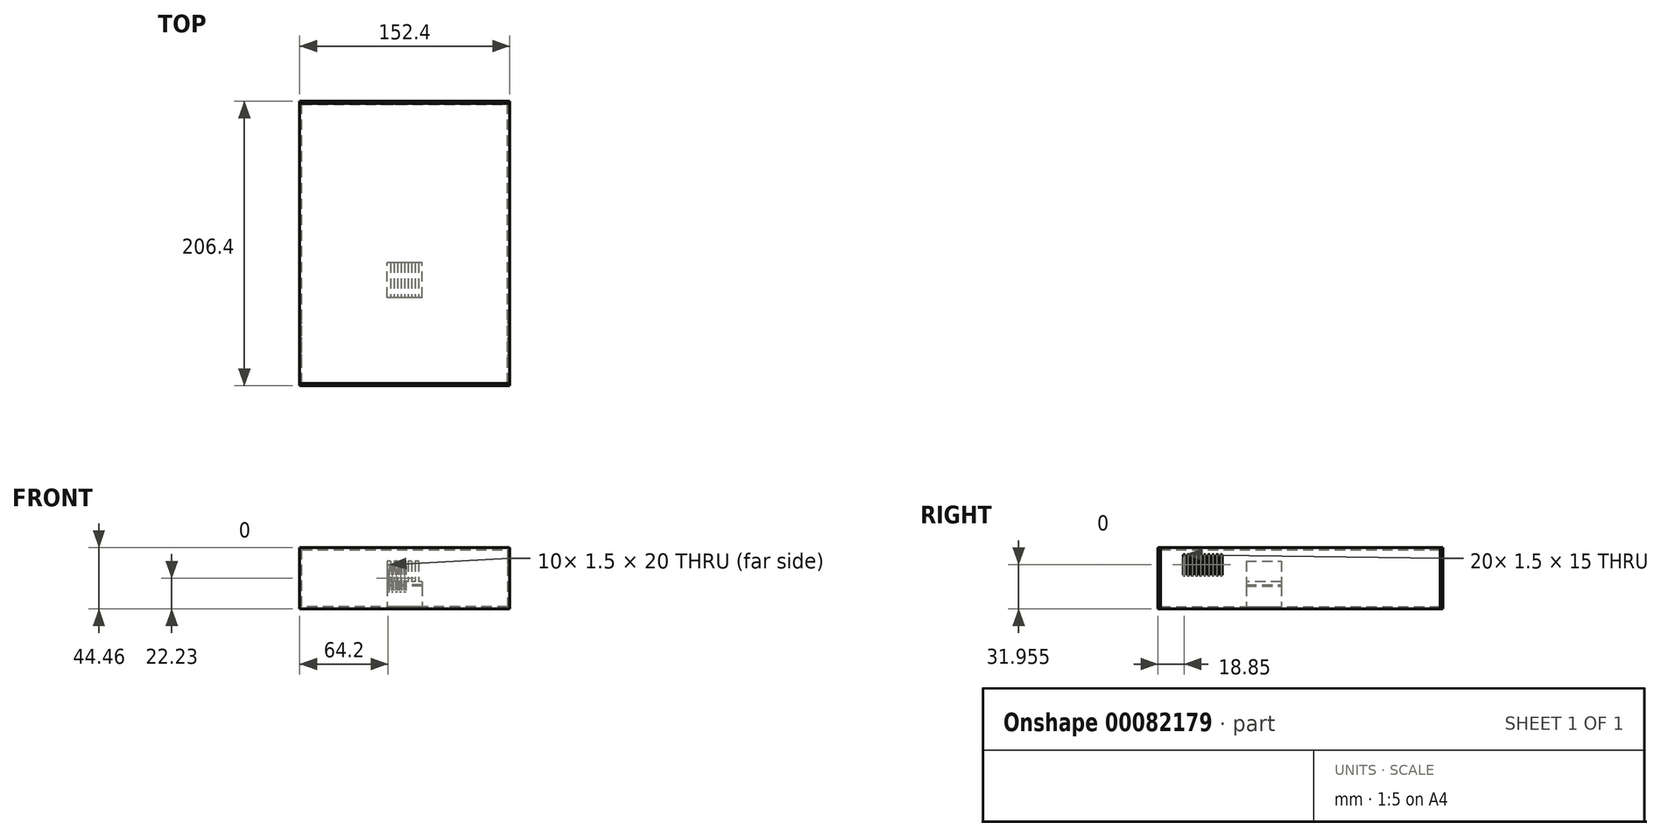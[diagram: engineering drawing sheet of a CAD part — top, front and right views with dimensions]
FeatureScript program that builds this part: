
annotation { "Feature Type Name" : "Feature", "Feature Type Description" : "" }
export const myFeature = defineFeature(function(context is Context, id is Id, definition is map)
    precondition{}
    {
        {
            var Q0;
            Q0=qCreatedBy(makeId("Front.planeOp"),FACE);
            var sketch = newSketch(context, id + "F0", { "sketchPlane" : qUnion([Q0])});
            skLineSegment(sketch, "E0.bottom", {"start": v(76.2, 22.22) * mm, "end": v(-76.2, 22.22) * mm});
            skLineSegment(sketch, "E0.top", {"start": v(76.2, -22.23) * mm, "end": v(-76.2, -22.23) * mm});
            skLineSegment(sketch, "E0.left", {"start": v(76.2, 22.22) * mm, "end": v(76.2, -22.23) * mm});
            skLineSegment(sketch, "E0.right", {"start": v(-76.2, 22.22) * mm, "end": v(-76.2, -22.23) * mm});
            skPoint(sketch, "E0.middle", {"position": v(0, 0) * mm});
            skSolve(sketch);
        }
        {
            var Q0;
            Q0 = qSketchRegion(id + "F0", true);
            extrude(context, id + "F1", {"entities" : qUnion([Q0]), "oppositeDirection" : true, "depth" : 203.2 * mm});
        }
        {
            var Q0;
            Q0=makeQuery(id+"F1.opExtrude","CAP_FACE",FACE,{"disambiguationData":[OSD([sQuery(id+"F0.wireOp",EDGE,"E0.bottom"),sQuery(id+"F0.wireOp",EDGE,"E0.top"),sQuery(id+"F0.wireOp",EDGE,"E0.left"),sQuery(id+"F0.wireOp",EDGE,"E0.right")])],"isStart":false});
            var sketch = newSketch(context, id + "F2", { "sketchPlane" : qUnion([Q0])});
            skLineSegment(sketch, "E1.0", {"start": v(-74.6, -20.62) * mm, "end": v(-74.6, 20.62) * mm});
            skLineSegment(sketch, "E1.1", {"start": v(74.6, -20.62) * mm, "end": v(-74.6, -20.62) * mm});
            skLineSegment(sketch, "E1.2", {"start": v(74.6, 20.62) * mm, "end": v(74.6, -20.62) * mm});
            skLineSegment(sketch, "E1.3", {"start": v(-74.6, 20.62) * mm, "end": v(74.6, 20.62) * mm});
            skSolve(sketch);
        }
        {
            var Q0;
            Q0 = qSketchRegion(id + "F2", true);
            extrude(context, id + "F3", {"entities" : qUnion([Q0]), "operationType" : NewBodyOperationType.REMOVE, "endBound" : BoundingType.THROUGH_ALL, "oppositeDirection" : true, "depth" : 25 * mm});
        }
        {
            var Q0;
            Q0=makeQuery(id+"F1.opExtrude","CAP_FACE",FACE,{"disambiguationData":[OSD([sQuery(id+"F0.wireOp",EDGE,"E0.bottom"),sQuery(id+"F0.wireOp",EDGE,"E0.top"),sQuery(id+"F0.wireOp",EDGE,"E0.left"),sQuery(id+"F0.wireOp",EDGE,"E0.right")])],"isStart":false});
            var sketch = newSketch(context, id + "F4", { "sketchPlane" : qUnion([Q0])});
            skSolve(sketch);
        }
        {
            var Q0;
            Q0=makeQuery(id+"F4.imprint","IMPRINT",FACE,{"disambiguationData":[TD([[makeQuery(id+"F4.imprint","IMPRINT",EDGE,{"derivedFrom":makeQuery(id+"F1.opExtrude","CAP_EDGE",EDGE,{"disambiguationData":[OSD([sQuery(id+"F0.wireOp",EDGE,"E0.bottom")])],"isStart":false})}),-1.0]])]});
            var sketch = newSketch(context, id + "F5", { "sketchPlane" : qUnion([Q0])});
            skLineSegment(sketch, "E2.0", {"start": v(-76.2, 22.22) * mm, "end": v(76.2, 22.22) * mm});
            skLineSegment(sketch, "E3.0", {"start": v(76.2, 22.22) * mm, "end": v(76.2, -22.23) * mm});
            skLineSegment(sketch, "E4.0", {"start": v(-76.2, -22.23) * mm, "end": v(76.2, -22.23) * mm});
            skLineSegment(sketch, "E5.0", {"start": v(-76.2, 22.22) * mm, "end": v(-76.2, -22.23) * mm});
            skSolve(sketch);
        }
        {
            var Q0;
            Q0 = qSketchRegion(id + "F5", true);
            var Q1;
            Q1=makeQuery(id+"F4.imprint","IMPRINT",FACE,{"disambiguationData":[TD([[makeQuery(id+"F4.imprint","IMPRINT",EDGE,{"derivedFrom":makeQuery(id+"F3.boolean.opBoolean","COPY",EDGE,{"derivedFrom":makeQuery(id+"F3.opExtrude","CAP_EDGE",EDGE,{"disambiguationData":[OSD([sQuery(id+"F2.wireOp",EDGE,"E1.0")])],"isStart":true})})}),-1.0]])]});
            extrude(context, id + "F6", {"entities" : qUnion([Q0, Q1]), "operationType" : NewBodyOperationType.ADD, "oppositeDirection" : true, "depth" : .63 * mm});
        }
        {
            var Q0;
            Q0=makeQuery(id+"F1.opExtrude","CAP_FACE",FACE,{"disambiguationData":[OSD([sQuery(id+"F0.wireOp",EDGE,"E0.bottom"),sQuery(id+"F0.wireOp",EDGE,"E0.top"),sQuery(id+"F0.wireOp",EDGE,"E0.left"),sQuery(id+"F0.wireOp",EDGE,"E0.right")])],"isStart":false});
            var sketch = newSketch(context, id + "F7", { "sketchPlane" : qUnion([Q0])});
            skLineSegment(sketch, "E6.0", {"start": v(-76.2, 22.22) * mm, "end": v(-76.2, -22.23) * mm});
            skLineSegment(sketch, "E6.1", {"start": v(-76.2, 22.22) * mm, "end": v(76.2, 22.22) * mm});
            skLineSegment(sketch, "E6.2", {"start": v(76.2, 22.22) * mm, "end": v(76.2, -22.23) * mm});
            skLineSegment(sketch, "E6.3", {"start": v(-76.2, -22.23) * mm, "end": v(76.2, -22.23) * mm});
            skSolve(sketch);
        }
        {
            var Q0;
            Q0 = qSketchRegion(id + "F7", true);
            extrude(context, id + "F8", {"entities" : qUnion([Q0]), "depth" : 1.6 * mm});
        }
        {
            var Q0;
            Q0=makeQuery(id+"F1.opExtrude","CAP_FACE",FACE,{"disambiguationData":[OSD([sQuery(id+"F0.wireOp",EDGE,"E0.bottom"),sQuery(id+"F0.wireOp",EDGE,"E0.top"),sQuery(id+"F0.wireOp",EDGE,"E0.left"),sQuery(id+"F0.wireOp",EDGE,"E0.right")])],"isStart":true});
            var sketch = newSketch(context, id + "F9", { "sketchPlane" : qUnion([Q0])});
            skLineSegment(sketch, "E7.0.0", {"start": v(76.2, -22.23) * mm, "end": v(76.2, 22.22) * mm});
            skLineSegment(sketch, "E7.0.1", {"start": v(76.2, 22.22) * mm, "end": v(-76.2, 22.22) * mm});
            skLineSegment(sketch, "E7.0.2", {"start": v(-76.2, 22.22) * mm, "end": v(-76.2, -22.23) * mm});
            skLineSegment(sketch, "E7.0.3", {"start": v(-76.2, -22.23) * mm, "end": v(76.2, -22.23) * mm});
            skSolve(sketch);
        }
        {
            var Q0;
            Q0 = qSketchRegion(id + "F9", true);
            extrude(context, id + "F10", {"entities" : qUnion([Q0]), "depth" : 1.6 * mm});
        }
        {
            var Q0;
            Q0=makeQuery(id+"F1.opExtrude","SWEPT_FACE",FACE,{"disambiguationData":[OSD([sQuery(id+"F0.wireOp",EDGE,"E0.right")])]});
            var sketch = newSketch(context, id + "F11", { "sketchPlane" : qUnion([Q0])});
            skLineSegment(sketch, "E8.bottom", {"start": v(-45, 17.22) * mm, "end": v(-43.5, 17.22) * mm});
            skLineSegment(sketch, "E8.top", {"start": v(-45, 2.22) * mm, "end": v(-43.5, 2.22) * mm});
            skLineSegment(sketch, "E8.left", {"start": v(-45, 17.22) * mm, "end": v(-45, 2.22) * mm});
            skLineSegment(sketch, "E8.right", {"start": v(-43.5, 17.22) * mm, "end": v(-43.5, 2.22) * mm});
            skLineSegment(sketch, "E9.1.0.0", {"start": v(-40.5, 17.22) * mm, "end": v(-40.5, 2.22) * mm});
            skLineSegment(sketch, "E9.1.0.1", {"start": v(-42, 17.22) * mm, "end": v(-42, 2.22) * mm});
            skLineSegment(sketch, "E9.1.0.2", {"start": v(-42, 2.22) * mm, "end": v(-40.5, 2.22) * mm});
            skLineSegment(sketch, "E9.1.0.3", {"start": v(-42, 17.22) * mm, "end": v(-40.5, 17.22) * mm});
            skLineSegment(sketch, "E9.2.0.0", {"start": v(-37.5, 17.22) * mm, "end": v(-37.5, 2.22) * mm});
            skLineSegment(sketch, "E9.2.0.1", {"start": v(-39, 17.22) * mm, "end": v(-39, 2.22) * mm});
            skLineSegment(sketch, "E9.2.0.2", {"start": v(-39, 2.22) * mm, "end": v(-37.5, 2.22) * mm});
            skLineSegment(sketch, "E9.2.0.3", {"start": v(-39, 17.22) * mm, "end": v(-37.5, 17.22) * mm});
            skLineSegment(sketch, "E9.3.0.0", {"start": v(-34.5, 17.22) * mm, "end": v(-34.5, 2.22) * mm});
            skLineSegment(sketch, "E9.3.0.1", {"start": v(-36, 17.22) * mm, "end": v(-36, 2.22) * mm});
            skLineSegment(sketch, "E9.3.0.2", {"start": v(-36, 2.22) * mm, "end": v(-34.5, 2.22) * mm});
            skLineSegment(sketch, "E9.3.0.3", {"start": v(-36, 17.22) * mm, "end": v(-34.5, 17.22) * mm});
            skLineSegment(sketch, "E9.4.0.0", {"start": v(-31.5, 17.22) * mm, "end": v(-31.5, 2.22) * mm});
            skLineSegment(sketch, "E9.4.0.1", {"start": v(-33, 17.22) * mm, "end": v(-33, 2.22) * mm});
            skLineSegment(sketch, "E9.4.0.2", {"start": v(-33, 2.22) * mm, "end": v(-31.5, 2.22) * mm});
            skLineSegment(sketch, "E9.4.0.3", {"start": v(-33, 17.22) * mm, "end": v(-31.5, 17.22) * mm});
            skLineSegment(sketch, "E9.5.0.0", {"start": v(-28.5, 17.22) * mm, "end": v(-28.5, 2.22) * mm});
            skLineSegment(sketch, "E9.5.0.1", {"start": v(-30, 17.22) * mm, "end": v(-30, 2.22) * mm});
            skLineSegment(sketch, "E9.5.0.2", {"start": v(-30, 2.22) * mm, "end": v(-28.5, 2.22) * mm});
            skLineSegment(sketch, "E9.5.0.3", {"start": v(-30, 17.22) * mm, "end": v(-28.5, 17.22) * mm});
            skLineSegment(sketch, "E9.6.0.0", {"start": v(-25.5, 17.22) * mm, "end": v(-25.5, 2.22) * mm});
            skLineSegment(sketch, "E9.6.0.1", {"start": v(-27, 17.22) * mm, "end": v(-27, 2.22) * mm});
            skLineSegment(sketch, "E9.6.0.2", {"start": v(-27, 2.22) * mm, "end": v(-25.5, 2.22) * mm});
            skLineSegment(sketch, "E9.6.0.3", {"start": v(-27, 17.22) * mm, "end": v(-25.5, 17.22) * mm});
            skLineSegment(sketch, "E9.7.0.0", {"start": v(-22.5, 17.22) * mm, "end": v(-22.5, 2.22) * mm});
            skLineSegment(sketch, "E9.7.0.1", {"start": v(-24, 17.22) * mm, "end": v(-24, 2.22) * mm});
            skLineSegment(sketch, "E9.7.0.2", {"start": v(-24, 2.22) * mm, "end": v(-22.5, 2.22) * mm});
            skLineSegment(sketch, "E9.7.0.3", {"start": v(-24, 17.22) * mm, "end": v(-22.5, 17.22) * mm});
            skLineSegment(sketch, "E9.8.0.0", {"start": v(-19.5, 17.22) * mm, "end": v(-19.5, 2.22) * mm});
            skLineSegment(sketch, "E9.8.0.1", {"start": v(-21, 17.22) * mm, "end": v(-21, 2.22) * mm});
            skLineSegment(sketch, "E9.8.0.2", {"start": v(-21, 2.22) * mm, "end": v(-19.5, 2.22) * mm});
            skLineSegment(sketch, "E9.8.0.3", {"start": v(-21, 17.22) * mm, "end": v(-19.5, 17.22) * mm});
            skLineSegment(sketch, "E9.9.0.0", {"start": v(-16.5, 17.22) * mm, "end": v(-16.5, 2.22) * mm});
            skLineSegment(sketch, "E9.9.0.1", {"start": v(-18, 17.22) * mm, "end": v(-18, 2.22) * mm});
            skLineSegment(sketch, "E9.9.0.2", {"start": v(-18, 2.22) * mm, "end": v(-16.5, 2.22) * mm});
            skLineSegment(sketch, "E9.9.0.3", {"start": v(-18, 17.22) * mm, "end": v(-16.5, 17.22) * mm});
            skLineSegment(sketch, "E9.direction1", {"start": v(-43.5, 2.22) * mm, "end": v(-40.5, 2.22) * mm, "construction": true});
            skSolve(sketch);
        }
        {
            var Q0;
            Q0 = qSketchRegion(id + "F11", true);
            extrude(context, id + "F12", {"entities" : qUnion([Q0]), "operationType" : NewBodyOperationType.REMOVE, "endBound" : BoundingType.THROUGH_ALL, "oppositeDirection" : true, "depth" : 25 * mm});
        }
        {
            var Q0;
            Q0=makeQuery(id+"F3.boolean.opBoolean","COPY",FACE,{"derivedFrom":makeQuery(id+"F3.opExtrude","SWEPT_FACE",FACE,{"disambiguationData":[OSD([sQuery(id+"F2.wireOp",EDGE,"E1.1")])]})});
            var sketch = newSketch(context, id + "F13", { "sketchPlane" : qUnion([Q0])});
            skLineSegment(sketch, "E10.bottom", {"start": v(12.7, 62.3) * mm, "end": v(-12.7, 62.3) * mm});
            skLineSegment(sketch, "E10.top", {"start": v(12.7, 87.7) * mm, "end": v(-12.7, 87.7) * mm});
            skLineSegment(sketch, "E10.left", {"start": v(12.7, 62.3) * mm, "end": v(12.7, 87.7) * mm});
            skLineSegment(sketch, "E10.right", {"start": v(-12.7, 62.3) * mm, "end": v(-12.7, 87.7) * mm});
            skPoint(sketch, "E10.middle", {"position": v(0, 75) * mm});
            skLineSegment(sketch, "E11", {"start": v(0, 75) * mm, "end": v(0, 0) * mm, "construction": true});
            skSolve(sketch);
        }
        {
            var Q0;
            Q0 = qSketchRegion(id + "F13", true);
            extrude(context, id + "F14", {"entities" : qUnion([Q0]), "depth" : 15 * mm});
        }
        {
            var Q0;
            Q0=makeQuery(id+"F14.opExtrude","CAP_FACE",FACE,{"disambiguationData":[OSD([sQuery(id+"F13.wireOp",EDGE,"E10.bottom"),sQuery(id+"F13.wireOp",EDGE,"E10.top"),sQuery(id+"F13.wireOp",EDGE,"E10.left"),sQuery(id+"F13.wireOp",EDGE,"E10.right")])],"isStart":false});
            var sketch = newSketch(context, id + "F15", { "sketchPlane" : qUnion([Q0])});
            skLineSegment(sketch, "E12.0.0", {"start": v(-12.7, 62.3) * mm, "end": v(12.7, 62.3) * mm});
            skLineSegment(sketch, "E12.0.1", {"start": v(12.7, 62.3) * mm, "end": v(12.7, 87.7) * mm});
            skLineSegment(sketch, "E12.0.2", {"start": v(12.7, 87.7) * mm, "end": v(-12.7, 87.7) * mm});
            skLineSegment(sketch, "E12.0.3", {"start": v(-12.7, 87.7) * mm, "end": v(-12.7, 62.3) * mm});
            skSolve(sketch);
        }
        {
            var Q0;
            Q0 = qSketchRegion(id + "F15", true);
            extrude(context, id + "F16", {"entities" : qUnion([Q0]), "depth" : 1 * mm});
        }
        {
            var Q0;
            Q0=makeQuery(id+"F16.opExtrude","CAP_FACE",FACE,{"disambiguationData":[OSD([sQuery(id+"F15.wireOp",EDGE,"E12.0.0"),sQuery(id+"F15.wireOp",EDGE,"E12.0.1"),sQuery(id+"F15.wireOp",EDGE,"E12.0.2"),sQuery(id+"F15.wireOp",EDGE,"E12.0.3")])],"isStart":false});
            var sketch = newSketch(context, id + "F17", { "sketchPlane" : qUnion([Q0])});
            skLineSegment(sketch, "E13.0.0", {"start": v(-12.7, 62.3) * mm, "end": v(12.7, 62.3) * mm});
            skLineSegment(sketch, "E13.0.1", {"start": v(12.7, 62.3) * mm, "end": v(12.7, 87.7) * mm});
            skLineSegment(sketch, "E13.0.2", {"start": v(12.7, 87.7) * mm, "end": v(-12.7, 87.7) * mm});
            skLineSegment(sketch, "E13.0.3", {"start": v(-12.7, 87.7) * mm, "end": v(-12.7, 62.3) * mm});
            skSolve(sketch);
        }
        {
            var Q0;
            Q0 = qSketchRegion(id + "F17", true);
            extrude(context, id + "F18", {"entities" : qUnion([Q0]), "depth" : 2 * mm});
        }
        {
            var Q0;
            Q0=makeQuery(id+"F18.opExtrude","CAP_FACE",FACE,{"disambiguationData":[OSD([sQuery(id+"F17.wireOp",EDGE,"E13.0.0"),sQuery(id+"F17.wireOp",EDGE,"E13.0.1"),sQuery(id+"F17.wireOp",EDGE,"E13.0.2"),sQuery(id+"F17.wireOp",EDGE,"E13.0.3")])],"isStart":false});
            var sketch = newSketch(context, id + "F19", { "sketchPlane" : qUnion([Q0])});
            skLineSegment(sketch, "E14.bottom", {"start": v(-12.7, 87.7) * mm, "end": v(-10.16, 87.7) * mm});
            skLineSegment(sketch, "E14.top", {"start": v(-12.7, 62.3) * mm, "end": v(-10.16, 62.3) * mm});
            skLineSegment(sketch, "E14.left", {"start": v(-12.7, 87.7) * mm, "end": v(-12.7, 62.3) * mm});
            skLineSegment(sketch, "E14.right", {"start": v(-10.16, 87.7) * mm, "end": v(-10.16, 62.3) * mm});
            skLineSegment(sketch, "E15.1.0.0", {"start": v(-7.62, 87.7) * mm, "end": v(-5.08, 87.7) * mm});
            skLineSegment(sketch, "E15.1.0.1", {"start": v(-7.62, 62.3) * mm, "end": v(-5.08, 62.3) * mm});
            skLineSegment(sketch, "E15.1.0.2", {"start": v(-7.62, 87.7) * mm, "end": v(-7.62, 62.3) * mm});
            skLineSegment(sketch, "E15.1.0.3", {"start": v(-5.08, 87.7) * mm, "end": v(-5.08, 62.3) * mm});
            skLineSegment(sketch, "E15.2.0.0", {"start": v(-2.54, 87.7) * mm, "end": v(0, 87.7) * mm});
            skLineSegment(sketch, "E15.2.0.1", {"start": v(-2.54, 62.3) * mm, "end": v(0, 62.3) * mm});
            skLineSegment(sketch, "E15.2.0.2", {"start": v(-2.54, 87.7) * mm, "end": v(-2.54, 62.3) * mm});
            skLineSegment(sketch, "E15.2.0.3", {"start": v(0, 87.7) * mm, "end": v(0, 62.3) * mm});
            skLineSegment(sketch, "E15.3.0.0", {"start": v(2.54, 87.7) * mm, "end": v(5.08, 87.7) * mm});
            skLineSegment(sketch, "E15.3.0.1", {"start": v(2.54, 62.3) * mm, "end": v(5.08, 62.3) * mm});
            skLineSegment(sketch, "E15.3.0.2", {"start": v(2.54, 87.7) * mm, "end": v(2.54, 62.3) * mm});
            skLineSegment(sketch, "E15.3.0.3", {"start": v(5.08, 87.7) * mm, "end": v(5.08, 62.3) * mm});
            skLineSegment(sketch, "E15.4.0.0", {"start": v(7.62, 87.7) * mm, "end": v(10.16, 87.7) * mm});
            skLineSegment(sketch, "E15.4.0.1", {"start": v(7.62, 62.3) * mm, "end": v(10.16, 62.3) * mm});
            skLineSegment(sketch, "E15.4.0.2", {"start": v(7.62, 87.7) * mm, "end": v(7.62, 62.3) * mm});
            skLineSegment(sketch, "E15.4.0.3", {"start": v(10.16, 87.7) * mm, "end": v(10.16, 62.3) * mm});
            skLineSegment(sketch, "E15.direction1", {"start": v(-12.7, 87.7) * mm, "end": v(-7.62, 87.7) * mm, "construction": true});
            skSolve(sketch);
        }
        {
            var Q0;
            Q0=makeQuery(id+"F19.imprint","IMPRINT",FACE,{"disambiguationData":[TD([[makeQuery(id+"F19.imprint","IMPRINT",EDGE,{"derivedFrom":sQuery(id+"F19.wireOp",EDGE,"E14.bottom")}),1.0]])]});
            var Q1;
            Q1=makeQuery(id+"F19.imprint","IMPRINT",FACE,{"disambiguationData":[TD([[makeQuery(id+"F19.imprint","IMPRINT",EDGE,{"derivedFrom":sQuery(id+"F19.wireOp",EDGE,"E15.1.0.0")}),1.0]])]});
            var Q2;
            Q2=makeQuery(id+"F19.imprint","IMPRINT",FACE,{"disambiguationData":[TD([[makeQuery(id+"F19.imprint","IMPRINT",EDGE,{"derivedFrom":sQuery(id+"F19.wireOp",EDGE,"E15.2.0.0")}),1.0]])]});
            var Q3;
            Q3=makeQuery(id+"F19.imprint","IMPRINT",FACE,{"disambiguationData":[TD([[makeQuery(id+"F19.imprint","IMPRINT",EDGE,{"derivedFrom":sQuery(id+"F19.wireOp",EDGE,"E15.3.0.0")}),1.0]])]});
            var Q4;
            Q4=makeQuery(id+"F19.imprint","IMPRINT",FACE,{"disambiguationData":[TD([[makeQuery(id+"F19.imprint","IMPRINT",EDGE,{"derivedFrom":sQuery(id+"F19.wireOp",EDGE,"E15.4.0.0")}),1.0]])]});
            extrude(context, id + "F20", {"entities" : qUnion([Q0, Q1, Q2, Q3, Q4]), "operationType" : NewBodyOperationType.ADD, "depth" : 15 * mm});
        }
        {
            var Q0;
            Q0=makeQuery(id+"F8.opExtrude","CAP_FACE",FACE,{"disambiguationData":[OSD([sQuery(id+"F7.wireOp",EDGE,"E6.0"),sQuery(id+"F7.wireOp",EDGE,"E6.1"),sQuery(id+"F7.wireOp",EDGE,"E6.2"),sQuery(id+"F7.wireOp",EDGE,"E6.3")])],"isStart":false});
            var sketch = newSketch(context, id + "F21", { "sketchPlane" : qUnion([Q0])});
            skLineSegment(sketch, "E16.bottom", {"start": v(0.75, 10) * mm, "end": v(-0.75, 10) * mm});
            skLineSegment(sketch, "E16.top", {"start": v(0.75, -10) * mm, "end": v(-0.75, -10) * mm});
            skLineSegment(sketch, "E16.left", {"start": v(0.75, 10) * mm, "end": v(0.75, -10) * mm});
            skLineSegment(sketch, "E16.right", {"start": v(-0.75, 10) * mm, "end": v(-0.75, -10) * mm});
            skPoint(sketch, "E16.middle", {"position": v(0, 0) * mm});
            skLineSegment(sketch, "E17.1.0.0", {"start": v(2.25, 10) * mm, "end": v(2.25, -10) * mm});
            skLineSegment(sketch, "E17.1.0.1", {"start": v(3.75, 10) * mm, "end": v(3.75, -10) * mm});
            skPoint(sketch, "E17.1.0.2", {"position": v(3, 0) * mm});
            skLineSegment(sketch, "E17.1.0.3", {"start": v(3.75, -10) * mm, "end": v(2.25, -10) * mm});
            skLineSegment(sketch, "E17.1.0.4", {"start": v(3.75, 10) * mm, "end": v(2.25, 10) * mm});
            skLineSegment(sketch, "E17.2.0.0", {"start": v(5.25, 10) * mm, "end": v(5.25, -10) * mm});
            skLineSegment(sketch, "E17.2.0.1", {"start": v(6.75, 10) * mm, "end": v(6.75, -10) * mm});
            skPoint(sketch, "E17.2.0.2", {"position": v(6, 0) * mm});
            skLineSegment(sketch, "E17.2.0.3", {"start": v(6.75, -10) * mm, "end": v(5.25, -10) * mm});
            skLineSegment(sketch, "E17.2.0.4", {"start": v(6.75, 10) * mm, "end": v(5.25, 10) * mm});
            skLineSegment(sketch, "E17.3.0.0", {"start": v(8.25, 10) * mm, "end": v(8.25, -10) * mm});
            skLineSegment(sketch, "E17.3.0.1", {"start": v(9.75, 10) * mm, "end": v(9.75, -10) * mm});
            skPoint(sketch, "E17.3.0.2", {"position": v(9, 0) * mm});
            skLineSegment(sketch, "E17.3.0.3", {"start": v(9.75, -10) * mm, "end": v(8.25, -10) * mm});
            skLineSegment(sketch, "E17.3.0.4", {"start": v(9.75, 10) * mm, "end": v(8.25, 10) * mm});
            skLineSegment(sketch, "E17.4.0.0", {"start": v(11.25, 10) * mm, "end": v(11.25, -10) * mm});
            skLineSegment(sketch, "E17.4.0.1", {"start": v(12.75, 10) * mm, "end": v(12.75, -10) * mm});
            skPoint(sketch, "E17.4.0.2", {"position": v(12, 0) * mm});
            skLineSegment(sketch, "E17.4.0.3", {"start": v(12.75, -10) * mm, "end": v(11.25, -10) * mm});
            skLineSegment(sketch, "E17.4.0.4", {"start": v(12.75, 10) * mm, "end": v(11.25, 10) * mm});
            skLineSegment(sketch, "E17.direction1", {"start": v(-0.75, -10) * mm, "end": v(2.25, -10) * mm, "construction": true});
            skSolve(sketch);
        }
        {
            var Q0;
            Q0 = qSketchRegion(id + "F21", true);
            extrude(context, id + "F22", {"entities" : qUnion([Q0]), "operationType" : NewBodyOperationType.REMOVE, "oppositeDirection" : true, "depth" : 25 * mm});
        }
    });
